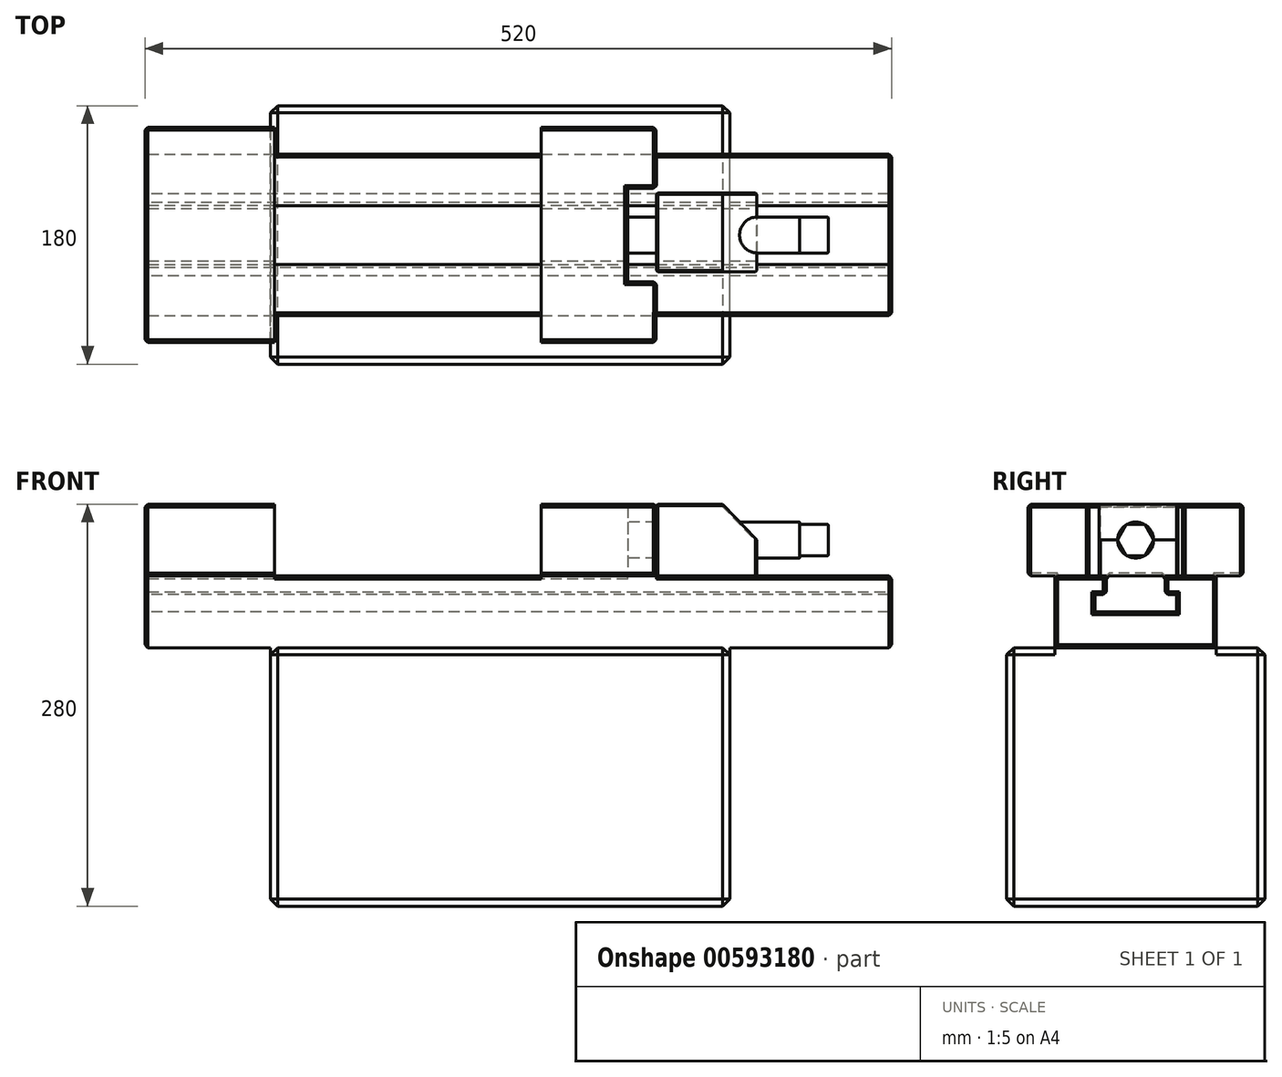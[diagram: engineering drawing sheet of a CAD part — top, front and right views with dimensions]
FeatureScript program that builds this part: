
annotation { "Feature Type Name" : "Feature", "Feature Type Description" : "" }
export const myFeature = defineFeature(function(context is Context, id is Id, definition is map)
    precondition{}
    {
        {
            var Q0;
            Q0=qCreatedBy(makeId("Top.planeOp"),FACE);
            var sketch = newSketch(context, id + "F0", { "sketchPlane" : qUnion([Q0])});
            skLineSegment(sketch, "E0.bottom", {"start": v(-189.84, -90) * mm, "end": v(130.16, -90) * mm});
            skLineSegment(sketch, "E0.top", {"start": v(-189.84, 90) * mm, "end": v(130.16, 90) * mm});
            skLineSegment(sketch, "E0.left", {"start": v(-189.84, -90) * mm, "end": v(-189.84, 90) * mm});
            skLineSegment(sketch, "E0.right", {"start": v(130.16, -90) * mm, "end": v(130.16, 90) * mm});
            skSolve(sketch);
        }
        {
            var Q0;
            Q0 = qSketchRegion(id + "F0", true);
            extrude(context, id + "F1", {"entities" : qUnion([Q0]), "depth" : 180 * mm, "offsetDistance" : 25 * mm});
        }
        {
            var Q0;
            Q0=makeQuery(id+"F1.opExtrude","CAP_FACE",FACE,{"disambiguationData":[OSD([sQuery(id+"F0.wireOp",EDGE,"E0.bottom"),sQuery(id+"F0.wireOp",EDGE,"E0.top"),sQuery(id+"F0.wireOp",EDGE,"E0.left"),sQuery(id+"F0.wireOp",EDGE,"E0.right")])],"isStart":false});
            var sketch = newSketch(context, id + "F2", { "sketchPlane" : qUnion([Q0])});
            skLineSegment(sketch, "E1.bottom", {"start": v(-277.14, -56.25) * mm, "end": v(242.86, -56.25) * mm});
            skLineSegment(sketch, "E1.top", {"start": v(-277.14, 56.25) * mm, "end": v(242.86, 56.25) * mm});
            skLineSegment(sketch, "E1.left", {"start": v(-277.14, -56.25) * mm, "end": v(-277.14, 56.25) * mm});
            skLineSegment(sketch, "E1.right", {"start": v(242.86, -56.25) * mm, "end": v(242.86, 56.25) * mm});
            skSolve(sketch);
        }
        {
            var Q0;
            Q0 = qSketchRegion(id + "F2", true);
            extrude(context, id + "F3", {"entities" : qUnion([Q0]), "operationType" : NewBodyOperationType.ADD, "depth" : 50 * mm, "offsetDistance" : 25 * mm});
        }
        {
            var Q0;
            Q0=makeQuery(id+"F3.opExtrude","CAP_FACE",FACE,{"disambiguationData":[OSD([sQuery(id+"F2.wireOp",EDGE,"E1.bottom"),sQuery(id+"F2.wireOp",EDGE,"E1.top"),sQuery(id+"F2.wireOp",EDGE,"E1.left"),sQuery(id+"F2.wireOp",EDGE,"E1.right")])],"isStart":false});
            var sketch = newSketch(context, id + "F4", { "sketchPlane" : qUnion([Q0])});
            skLineSegment(sketch, "E2.bottom", {"start": v(-277.14, -75) * mm, "end": v(-187.14, -75) * mm});
            skLineSegment(sketch, "E2.top", {"start": v(-277.14, 75) * mm, "end": v(-187.14, 75) * mm});
            skLineSegment(sketch, "E2.left", {"start": v(-277.14, -75) * mm, "end": v(-277.14, 75) * mm});
            skLineSegment(sketch, "E2.right", {"start": v(-187.14, -75) * mm, "end": v(-187.14, 75) * mm});
            skSolve(sketch);
        }
        {
            var Q0;
            Q0 = qSketchRegion(id + "F4", true);
            extrude(context, id + "F5", {"entities" : qUnion([Q0]), "operationType" : NewBodyOperationType.ADD, "depth" : 50 * mm, "offsetDistance" : 25 * mm});
        }
        {
            var Q0;
            {var subQ5=sQuery(id+"F2.wireOp",EDGE,"E1.top");var subQ6=sQuery(id+"F2.wireOp",EDGE,"E1.right");var subQ7=sQuery(id+"F2.wireOp",EDGE,"E1.bottom");Q0=makeQuery(id+"F11.boolean.opBoolean","SPLIT",FACE,{"disambiguationData":[TD([makeQuery(id+"F3.opExtrude","SWEPT_FACE",FACE,{"disambiguationData":[OSD([subQ6])]})])],"derivedFrom":makeQuery(id+"F3.opExtrude","CAP_FACE",FACE,{"disambiguationData":[OSD([subQ7,subQ5,sQuery(id+"F2.wireOp",EDGE,"E1.left"),subQ6])],"isStart":false})});}
            var sketch = newSketch(context, id + "F6", { "sketchPlane" : qUnion([Q0])});
            skLineSegment(sketch, "E3.bottom", {"start": v(78.92, 29.42) * mm, "end": v(148.92, 29.42) * mm});
            skLineSegment(sketch, "E3.top", {"start": v(78.92, -25.58) * mm, "end": v(148.92, -25.58) * mm});
            skLineSegment(sketch, "E3.left", {"start": v(78.92, 29.42) * mm, "end": v(78.92, -25.58) * mm});
            skLineSegment(sketch, "E3.right", {"start": v(148.92, 29.42) * mm, "end": v(148.92, -25.58) * mm});
            skSolve(sketch);
        }
        {
            var Q0;
            Q0 = qSketchRegion(id + "F6", true);
            extrude(context, id + "F7", {"entities" : qUnion([Q0]), "operationType" : NewBodyOperationType.ADD, "depth" : 50 * mm, "offsetDistance" : 25 * mm});
        }
        {
            var Q0;
            Q0=makeQuery(id+"F7.opExtrude","SWEPT_FACE",FACE,{"disambiguationData":[OSD([sQuery(id+"F6.wireOp",EDGE,"E3.top")])]});
            var sketch = newSketch(context, id + "F8", { "sketchPlane" : qUnion([Q0])});
            skLineSegment(sketch, "E4", {"start": v(125, 280) * mm, "end": v(148.92, 255) * mm});
            skLineSegment(sketch, "E5", {"start": v(148.92, 255) * mm, "end": v(148.92, 280) * mm});
            skLineSegment(sketch, "E6", {"start": v(148.92, 280) * mm, "end": v(125, 280) * mm});
            skSolve(sketch);
        }
        {
            var Q0;
            Q0 = qSketchRegion(id + "F8", true);
            extrude(context, id + "F9", {"entities" : qUnion([Q0]), "operationType" : NewBodyOperationType.REMOVE, "endBound" : BoundingType.THROUGH_ALL, "oppositeDirection" : true, "depth" : 25 * mm, "offsetDistance" : 25 * mm});
        }
        {
            var Q0;
            Q0=makeQuery(id+"F3.opExtrude","CAP_FACE",FACE,{"disambiguationData":[OSD([sQuery(id+"F2.wireOp",EDGE,"E1.bottom"),sQuery(id+"F2.wireOp",EDGE,"E1.top"),sQuery(id+"F2.wireOp",EDGE,"E1.left"),sQuery(id+"F2.wireOp",EDGE,"E1.right")])],"isStart":false});
            var sketch = newSketch(context, id + "F10", { "sketchPlane" : qUnion([Q0])});
            skLineSegment(sketch, "E7.bottom", {"start": v(-1.14, -75) * mm, "end": v(78.86, -75) * mm});
            skLineSegment(sketch, "E7.top", {"start": v(-1.14, 75) * mm, "end": v(78.86, 75) * mm});
            skLineSegment(sketch, "E7.left", {"start": v(-1.14, -75) * mm, "end": v(-1.14, 75) * mm});
            skLineSegment(sketch, "E8", {"start": v(58.92, -32.5) * mm, "end": v(79.04, -32.5) * mm});
            skLineSegment(sketch, "E9", {"start": v(58.92, -32.5) * mm, "end": v(58.92, 32.5) * mm});
            skLineSegment(sketch, "E10", {"start": v(58.92, 32.5) * mm, "end": v(78.92, 32.5) * mm});
            skLineSegment(sketch, "E11.trimOffspring", {"start": v(78.92, 32.5) * mm, "end": v(78.86, 75) * mm});
            skLineSegment(sketch, "E12", {"start": v(78.86, -75) * mm, "end": v(79.04, -32.5) * mm});
            skSolve(sketch);
        }
        {
            var Q0;
            Q0 = qSketchRegion(id + "F10", true);
            extrude(context, id + "F11", {"entities" : qUnion([Q0]), "operationType" : NewBodyOperationType.ADD, "depth" : 50 * mm, "offsetDistance" : 25 * mm});
        }
        {
            var Q0;
            Q0=makeQuery(id+"F11.opExtrude","SWEPT_FACE",FACE,{"disambiguationData":[OSD([sQuery(id+"F10.wireOp",EDGE,"E9")])]});
            var sketch = newSketch(context, id + "F12", { "sketchPlane" : qUnion([Q0])});
            skLineSegment(sketch, "E13", {"start": v(-32.5, 230) * mm, "end": v(32.5, 280) * mm});
            skCircle(sketch, "E14", {"center": v(0, 255) * mm, "radius": 12.5 * mm});
            skSolve(sketch);
        }
        {
            var Q0;
            Q0 = qSketchRegion(id + "F12", true);
            extrude(context, id + "F13", {"entities" : qUnion([Q0]), "operationType" : NewBodyOperationType.ADD, "depth" : 120 * mm, "offsetDistance" : 25 * mm});
        }
        {
            var Q0;
            Q0=makeQuery(id+"F13.opExtrude","CAP_FACE",FACE,{"disambiguationData":[OSD([sQuery(id+"F12.wireOp",EDGE,"E14")])],"isStart":false});
            var sketch = newSketch(context, id + "F14", { "sketchPlane" : qUnion([Q0])});
            skCircle(sketch, "E15.cCircle", {"center": v(0, 255) * mm, "radius": 11 * mm, "construction": true});
            skLineSegment(sketch, "E15.0", {"start": v(6.35, 244) * mm, "end": v(-6.35, 244) * mm});
            skLineSegment(sketch, "E15.1", {"start": v(-6.35, 244) * mm, "end": v(-12.7, 255) * mm});
            skLineSegment(sketch, "E15.2", {"start": v(-12.7, 255) * mm, "end": v(-6.35, 266) * mm});
            skLineSegment(sketch, "E15.3", {"start": v(-6.35, 266) * mm, "end": v(6.35, 266) * mm});
            skLineSegment(sketch, "E15.4", {"start": v(6.35, 266) * mm, "end": v(12.7, 255) * mm});
            skLineSegment(sketch, "E15.5", {"start": v(12.7, 255) * mm, "end": v(6.35, 244) * mm});
            skPoint(sketch, "E15.0.midPoint", {"position": v(0, 244) * mm});
            skSolve(sketch);
        }
        {
            var Q0;
            Q0 = qSketchRegion(id + "F14", true);
            extrude(context, id + "F15", {"entities" : qUnion([Q0]), "operationType" : NewBodyOperationType.ADD, "depth" : 20 * mm, "offsetDistance" : 25 * mm});
        }
        {
            var Q0;
            Q0=makeQuery(id+"F15.opExtrude","CAP_FACE",FACE,{"disambiguationData":[OSD([sQuery(id+"F14.wireOp",EDGE,"E15.0"),sQuery(id+"F14.wireOp",EDGE,"E15.1"),sQuery(id+"F14.wireOp",EDGE,"E15.2"),sQuery(id+"F14.wireOp",EDGE,"E15.3"),sQuery(id+"F14.wireOp",EDGE,"E15.4"),sQuery(id+"F14.wireOp",EDGE,"E15.5")])],"isStart":false});
            var Q1;
            Q1=makeQuery(id+"F15.opExtrude","SWEPT_EDGE",EDGE,{"disambiguationData":[OSD([sQuery(id+"F14.wireOp",EDGE,"E15.2"),sQuery(id+"F14.wireOp",EDGE,"E15.3")])]});
            var Q2;
            Q2=makeQuery(id+"F15.opExtrude","SWEPT_EDGE",EDGE,{"disambiguationData":[OSD([sQuery(id+"F14.wireOp",EDGE,"E15.1"),sQuery(id+"F14.wireOp",EDGE,"E15.2")])]});
            var Q3;
            Q3=makeQuery(id+"F15.opExtrude","SWEPT_EDGE",EDGE,{"disambiguationData":[OSD([sQuery(id+"F14.wireOp",EDGE,"E15.3"),sQuery(id+"F14.wireOp",EDGE,"E15.4")])]});
            var Q4;
            Q4=makeQuery(id+"F15.opExtrude","SWEPT_EDGE",EDGE,{"disambiguationData":[OSD([sQuery(id+"F14.wireOp",EDGE,"E15.0"),sQuery(id+"F14.wireOp",EDGE,"E15.1")])]});
            var Q5;
            Q5=makeQuery(id+"F15.opExtrude","SWEPT_EDGE",EDGE,{"disambiguationData":[OSD([sQuery(id+"F14.wireOp",EDGE,"E15.0"),sQuery(id+"F14.wireOp",EDGE,"E15.5")])]});
            var Q6;
            Q6=makeQuery(id+"F15.opExtrude","SWEPT_EDGE",EDGE,{"disambiguationData":[OSD([sQuery(id+"F14.wireOp",EDGE,"E15.4"),sQuery(id+"F14.wireOp",EDGE,"E15.5")])]});
            fillet(context, id + "F16", {"entities" : qUnion([Q0, Q1, Q2, Q3, Q4, Q5, Q6]), "radius" : 1 * mm, "tangentPropagation" : true, "allowEdgeOverflow" : false});
        }
        {
            var Q0;
            Q0=makeQuery(id+"F7.opExtrude","CAP_EDGE",EDGE,{"disambiguationData":[OSD([sQuery(id+"F6.wireOp",EDGE,"E3.top")])],"isStart":false});
            var Q1;
            Q1=makeQuery(id+"F9.boolean.opBoolean","COPY",EDGE,{"derivedFrom":makeQuery(id+"F9.opExtrude","CAP_EDGE",EDGE,{"disambiguationData":[OSD([sQuery(id+"F8.wireOp",EDGE,"E4")])],"isStart":true})});
            var Q2;
            Q2=makeQuery(id+"F7.opExtrude","SWEPT_EDGE",EDGE,{"disambiguationData":[OSD([sQuery(id+"F6.wireOp",EDGE,"E3.top"),sQuery(id+"F6.wireOp",EDGE,"E3.right")])]});
            var Q3;
            Q3=makeQuery(id+"F7.opExtrude","SWEPT_EDGE",EDGE,{"disambiguationData":[OSD([sQuery(id+"F6.wireOp",EDGE,"E3.top"),sQuery(id+"F6.wireOp",EDGE,"E3.left")])]});
            var Q4;
            Q4=makeQuery(id+"F7.opExtrude","CAP_EDGE",EDGE,{"disambiguationData":[OSD([sQuery(id+"F6.wireOp",EDGE,"E3.left")])],"isStart":false});
            var Q5;
            Q5=makeQuery(id+"F7.opExtrude","CAP_EDGE",EDGE,{"disambiguationData":[OSD([sQuery(id+"F6.wireOp",EDGE,"E3.bottom")])],"isStart":false});
            var Q6;
            Q6=makeQuery(id+"F9.boolean.opBoolean","INTERSECT",EDGE,{"derivedFrom":[makeQuery(id+"F7.opExtrude","SWEPT_FACE",FACE,{"disambiguationData":[OSD([sQuery(id+"F6.wireOp",EDGE,"E3.bottom")])]}),makeQuery(id+"F9.opExtrude","SWEPT_FACE",FACE,{"disambiguationData":[OSD([sQuery(id+"F8.wireOp",EDGE,"E4")])]})]});
            var Q7;
            Q7=makeQuery(id+"F7.opExtrude","SWEPT_EDGE",EDGE,{"disambiguationData":[OSD([sQuery(id+"F6.wireOp",EDGE,"E3.bottom"),sQuery(id+"F6.wireOp",EDGE,"E3.right")])]});
            var Q8;
            Q8=makeQuery(id+"F7.opExtrude","SWEPT_EDGE",EDGE,{"disambiguationData":[OSD([sQuery(id+"F6.wireOp",EDGE,"E3.bottom"),sQuery(id+"F6.wireOp",EDGE,"E3.left")])]});
            chamfer(context, id + "F17", {"entities" : qUnion([Q0, Q1, Q2, Q3, Q4, Q5, Q6, Q7, Q8]), "width" : 1 * mm, "tangentPropagation" : true});
        }
        {
            var Q0;
            Q0=makeQuery(id+"F1.opExtrude","CAP_EDGE",EDGE,{"disambiguationData":[OSD([sQuery(id+"F0.wireOp",EDGE,"E0.bottom")])],"isStart":false});
            var Q1;
            Q1=makeQuery(id+"F1.opExtrude","SWEPT_EDGE",EDGE,{"disambiguationData":[OSD([sQuery(id+"F0.wireOp",EDGE,"E0.bottom"),sQuery(id+"F0.wireOp",EDGE,"E0.right")])]});
            var Q2;
            {var subQ1=sQuery(id+"F0.wireOp",EDGE,"E0.right");var subQ2=makeQuery(id+"F1.opExtrude","SWEPT_FACE",FACE,{"disambiguationData":[OSD([subQ1])]});var subQ3=sQuery(id+"F0.wireOp",EDGE,"E0.bottom");var subQ4=makeQuery(id+"F1.opExtrude","CAP_FACE",FACE,{"disambiguationData":[OSD([subQ3,sQuery(id+"F0.wireOp",EDGE,"E0.top"),sQuery(id+"F0.wireOp",EDGE,"E0.left"),subQ1])],"isStart":false});Q2=makeQuery(id+"F3.boolean.opBoolean","SPLIT",EDGE,{"disambiguationData":[topologyDisambiguationEdgeConnected([subQ4,subQ2]),TD([makeQuery(id+"F1.opExtrude","SWEPT_FACE",FACE,{"disambiguationData":[OSD([subQ3])]})])],"derivedFrom":makeQuery(id+"F1.opExtrude","CAP_EDGE",EDGE,{"disambiguationData":[OSD([subQ1])],"isStart":false})});}
            var Q3;
            {var subQ1=sQuery(id+"F0.wireOp",EDGE,"E0.right");var subQ2=makeQuery(id+"F1.opExtrude","SWEPT_FACE",FACE,{"disambiguationData":[OSD([subQ1])]});var subQ3=sQuery(id+"F0.wireOp",EDGE,"E0.top");var subQ4=makeQuery(id+"F1.opExtrude","CAP_FACE",FACE,{"disambiguationData":[OSD([sQuery(id+"F0.wireOp",EDGE,"E0.bottom"),subQ3,sQuery(id+"F0.wireOp",EDGE,"E0.left"),subQ1])],"isStart":false});Q3=makeQuery(id+"F3.boolean.opBoolean","SPLIT",EDGE,{"disambiguationData":[topologyDisambiguationEdgeConnected([subQ4,subQ2]),TD([makeQuery(id+"F1.opExtrude","SWEPT_FACE",FACE,{"disambiguationData":[OSD([subQ3])]})])],"derivedFrom":makeQuery(id+"F1.opExtrude","CAP_EDGE",EDGE,{"disambiguationData":[OSD([subQ1])],"isStart":false})});}
            var Q4;
            Q4=makeQuery(id+"F1.opExtrude","SWEPT_EDGE",EDGE,{"disambiguationData":[OSD([sQuery(id+"F0.wireOp",EDGE,"E0.top"),sQuery(id+"F0.wireOp",EDGE,"E0.right")])]});
            var Q5;
            Q5=makeQuery(id+"F1.opExtrude","CAP_EDGE",EDGE,{"disambiguationData":[OSD([sQuery(id+"F0.wireOp",EDGE,"E0.top")])],"isStart":false});
            var Q6;
            Q6=makeQuery(id+"F1.opExtrude","CAP_EDGE",EDGE,{"disambiguationData":[OSD([sQuery(id+"F0.wireOp",EDGE,"E0.right")])],"isStart":true});
            var Q7;
            Q7=makeQuery(id+"F1.opExtrude","CAP_EDGE",EDGE,{"disambiguationData":[OSD([sQuery(id+"F0.wireOp",EDGE,"E0.bottom")])],"isStart":true});
            var Q8;
            Q8=makeQuery(id+"F1.opExtrude","SWEPT_EDGE",EDGE,{"disambiguationData":[OSD([sQuery(id+"F0.wireOp",EDGE,"E0.bottom"),sQuery(id+"F0.wireOp",EDGE,"E0.left")])]});
            var Q9;
            Q9=makeQuery(id+"F1.opExtrude","CAP_EDGE",EDGE,{"disambiguationData":[OSD([sQuery(id+"F0.wireOp",EDGE,"E0.left")])],"isStart":true});
            var Q10;
            Q10=makeQuery(id+"F1.opExtrude","CAP_EDGE",EDGE,{"disambiguationData":[OSD([sQuery(id+"F0.wireOp",EDGE,"E0.top")])],"isStart":true});
            var Q11;
            Q11=makeQuery(id+"F1.opExtrude","SWEPT_EDGE",EDGE,{"disambiguationData":[OSD([sQuery(id+"F0.wireOp",EDGE,"E0.top"),sQuery(id+"F0.wireOp",EDGE,"E0.left")])]});
            var Q12;
            {var subQ1=sQuery(id+"F0.wireOp",EDGE,"E0.left");var subQ2=makeQuery(id+"F1.opExtrude","SWEPT_FACE",FACE,{"disambiguationData":[OSD([subQ1])]});var subQ3=sQuery(id+"F0.wireOp",EDGE,"E0.top");var subQ4=makeQuery(id+"F1.opExtrude","CAP_FACE",FACE,{"disambiguationData":[OSD([sQuery(id+"F0.wireOp",EDGE,"E0.bottom"),subQ3,subQ1,sQuery(id+"F0.wireOp",EDGE,"E0.right")])],"isStart":false});Q12=makeQuery(id+"F3.boolean.opBoolean","SPLIT",EDGE,{"disambiguationData":[topologyDisambiguationEdgeConnected([subQ4,subQ2]),TD([makeQuery(id+"F1.opExtrude","SWEPT_FACE",FACE,{"disambiguationData":[OSD([subQ3])]})])],"derivedFrom":makeQuery(id+"F1.opExtrude","CAP_EDGE",EDGE,{"disambiguationData":[OSD([subQ1])],"isStart":false})});}
            var Q13;
            {var subQ1=sQuery(id+"F0.wireOp",EDGE,"E0.left");var subQ2=makeQuery(id+"F1.opExtrude","SWEPT_FACE",FACE,{"disambiguationData":[OSD([subQ1])]});var subQ3=sQuery(id+"F0.wireOp",EDGE,"E0.bottom");var subQ4=makeQuery(id+"F1.opExtrude","CAP_FACE",FACE,{"disambiguationData":[OSD([subQ3,sQuery(id+"F0.wireOp",EDGE,"E0.top"),subQ1,sQuery(id+"F0.wireOp",EDGE,"E0.right")])],"isStart":false});Q13=makeQuery(id+"F3.boolean.opBoolean","SPLIT",EDGE,{"disambiguationData":[topologyDisambiguationEdgeConnected([subQ4,subQ2]),TD([makeQuery(id+"F1.opExtrude","SWEPT_FACE",FACE,{"disambiguationData":[OSD([subQ3])]})])],"derivedFrom":makeQuery(id+"F1.opExtrude","CAP_EDGE",EDGE,{"disambiguationData":[OSD([subQ1])],"isStart":false})});}
            chamfer(context, id + "F18", {"entities" : qUnion([Q0, Q1, Q2, Q3, Q4, Q5, Q6, Q7, Q8, Q9, Q10, Q11, Q12, Q13]), "width" : 5 * mm, "tangentPropagation" : true});
        }
        {
            var Q0;
            Q0=makeQuery(id+"F5.boolean.opBoolean","MERGE",FACE,{"derivedFrom":[makeQuery(id+"F3.opExtrude","SWEPT_FACE",FACE,{"disambiguationData":[OSD([sQuery(id+"F2.wireOp",EDGE,"E1.left")])]}),makeQuery(id+"F5.opExtrude","SWEPT_FACE",FACE,{"disambiguationData":[OSD([sQuery(id+"F4.wireOp",EDGE,"E2.left")])]})]});
            var sketch = newSketch(context, id + "F19", { "sketchPlane" : qUnion([Q0])});
            skLineSegment(sketch, "E16", {"start": v(-20.5, 230) * mm, "end": v(20.5, 230) * mm});
            skLineSegment(sketch, "E17", {"start": v(20.5, 230) * mm, "end": v(20.5, 217) * mm});
            skLineSegment(sketch, "E18", {"start": v(20.5, 217) * mm, "end": v(28.5, 217) * mm});
            skLineSegment(sketch, "E19", {"start": v(28.5, 217) * mm, "end": v(28.5, 205) * mm});
            skLineSegment(sketch, "E20", {"start": v(28.5, 205) * mm, "end": v(-28.5, 205) * mm});
            skLineSegment(sketch, "E21", {"start": v(-28.5, 205) * mm, "end": v(-28.5, 217) * mm});
            skLineSegment(sketch, "E22", {"start": v(-28.5, 217) * mm, "end": v(-20.5, 217) * mm});
            skLineSegment(sketch, "E23", {"start": v(-20.5, 217) * mm, "end": v(-20.5, 230) * mm});
            skSolve(sketch);
        }
        {
            var Q0;
            Q0 = qSketchRegion(id + "F19", true);
            extrude(context, id + "F20", {"entities" : qUnion([Q0]), "operationType" : NewBodyOperationType.REMOVE, "endBound" : BoundingType.THROUGH_ALL, "oppositeDirection" : true, "depth" : 25 * mm, "offsetDistance" : 25 * mm});
        }
        {
            var Q0;
            Q0=makeQuery(id+"F3.opExtrude","SWEPT_FACE",FACE,{"disambiguationData":[OSD([sQuery(id+"F2.wireOp",EDGE,"E1.right")])]});
            var Q1;
            Q1=makeQuery(id+"F5.boolean.opBoolean","MERGE",FACE,{"derivedFrom":[makeQuery(id+"F3.opExtrude","SWEPT_FACE",FACE,{"disambiguationData":[OSD([sQuery(id+"F2.wireOp",EDGE,"E1.left")])]}),makeQuery(id+"F5.opExtrude","SWEPT_FACE",FACE,{"disambiguationData":[OSD([sQuery(id+"F4.wireOp",EDGE,"E2.left")])]})]});
            var Q2;
            Q2=makeQuery(id+"F5.opExtrude","CAP_EDGE",EDGE,{"disambiguationData":[OSD([sQuery(id+"F4.wireOp",EDGE,"E2.top")])],"isStart":false});
            var Q3;
            Q3=makeQuery(id+"F5.opExtrude","CAP_EDGE",EDGE,{"disambiguationData":[OSD([sQuery(id+"F4.wireOp",EDGE,"E2.bottom")])],"isStart":false});
            var Q4;
            Q4=makeQuery(id+"F11.opExtrude","CAP_EDGE",EDGE,{"disambiguationData":[OSD([sQuery(id+"F10.wireOp",EDGE,"E7.top")])],"isStart":false});
            var Q5;
            Q5=makeQuery(id+"F11.opExtrude","CAP_EDGE",EDGE,{"disambiguationData":[OSD([sQuery(id+"F10.wireOp",EDGE,"E11.trimOffspring")])],"isStart":false});
            var Q6;
            Q6=makeQuery(id+"F11.opExtrude","CAP_EDGE",EDGE,{"disambiguationData":[OSD([sQuery(id+"F10.wireOp",EDGE,"E10")])],"isStart":false});
            var Q7;
            Q7=makeQuery(id+"F11.opExtrude","CAP_EDGE",EDGE,{"disambiguationData":[OSD([sQuery(id+"F10.wireOp",EDGE,"E9")])],"isStart":false});
            var Q8;
            Q8=makeQuery(id+"F11.opExtrude","CAP_EDGE",EDGE,{"disambiguationData":[OSD([sQuery(id+"F10.wireOp",EDGE,"E8")])],"isStart":false});
            var Q9;
            Q9=makeQuery(id+"F11.opExtrude","CAP_EDGE",EDGE,{"disambiguationData":[OSD([sQuery(id+"F10.wireOp",EDGE,"E12")])],"isStart":false});
            var Q10;
            Q10=makeQuery(id+"F11.opExtrude","CAP_EDGE",EDGE,{"disambiguationData":[OSD([sQuery(id+"F10.wireOp",EDGE,"E7.bottom")])],"isStart":false});
            var Q11;
            Q11=makeQuery(id+"F5.opExtrude","CAP_EDGE",EDGE,{"disambiguationData":[OSD([sQuery(id+"F4.wireOp",EDGE,"E2.bottom")])],"isStart":true});
            var Q12;
            Q12=makeQuery(id+"F11.opExtrude","CAP_EDGE",EDGE,{"disambiguationData":[OSD([sQuery(id+"F10.wireOp",EDGE,"E7.bottom")])],"isStart":true});
            var Q13;
            Q13=makeQuery(id+"F11.opExtrude","SWEPT_EDGE",EDGE,{"disambiguationData":[OSD([sQuery(id+"F10.wireOp",EDGE,"E7.bottom"),sQuery(id+"F10.wireOp",EDGE,"E12")])]});
            var Q14;
            Q14=makeQuery(id+"F11.opExtrude","SWEPT_EDGE",EDGE,{"disambiguationData":[OSD([sQuery(id+"F10.wireOp",EDGE,"E8"),sQuery(id+"F10.wireOp",EDGE,"E12")])]});
            var Q15;
            Q15=makeQuery(id+"F11.opExtrude","SWEPT_EDGE",EDGE,{"disambiguationData":[OSD([sQuery(id+"F10.wireOp",EDGE,"E10"),sQuery(id+"F10.wireOp",EDGE,"E11.trimOffspring")])]});
            var Q16;
            Q16=makeQuery(id+"F11.opExtrude","SWEPT_EDGE",EDGE,{"disambiguationData":[OSD([sQuery(id+"F10.wireOp",EDGE,"E7.top"),sQuery(id+"F10.wireOp",EDGE,"E11.trimOffspring")])]});
            var Q17;
            Q17=makeQuery(id+"F11.opExtrude","CAP_EDGE",EDGE,{"disambiguationData":[OSD([sQuery(id+"F10.wireOp",EDGE,"E7.top")])],"isStart":true});
            var Q18;
            Q18=makeQuery(id+"F5.opExtrude","CAP_EDGE",EDGE,{"disambiguationData":[OSD([sQuery(id+"F4.wireOp",EDGE,"E2.top")])],"isStart":true});
            var Q19;
            {var subQ0=sQuery(id+"F19.wireOp",EDGE,"E16");var subQ1=sQuery(id+"F2.wireOp",EDGE,"E1.right");var subQ2=makeQuery(id+"F3.opExtrude","CAP_FACE",FACE,{"disambiguationData":[OSD([sQuery(id+"F2.wireOp",EDGE,"E1.bottom"),sQuery(id+"F2.wireOp",EDGE,"E1.top"),sQuery(id+"F2.wireOp",EDGE,"E1.left"),subQ1])],"isStart":false});var subQ3=sQuery(id+"F19.wireOp",EDGE,"E17");var subQ4=makeQuery(id+"F20.opExtrude","SWEPT_FACE",FACE,{"disambiguationData":[OSD([subQ3])]});Q19=makeQuery(id+"F20.boolean.opBoolean","COPY",EDGE,{"disambiguationData":[topologyDisambiguationEdgeConnected([subQ2,subQ4]),TD([makeQuery(id+"F3.opExtrude","SWEPT_FACE",FACE,{"disambiguationData":[OSD([subQ1])]})])],"derivedFrom":makeQuery(id+"F20.opExtrude","SWEPT_EDGE",EDGE,{"disambiguationData":[OSD([subQ0,subQ3])]})});}
            var Q20;
            {var subQ0=sQuery(id+"F19.wireOp",EDGE,"E16");var subQ1=sQuery(id+"F2.wireOp",EDGE,"E1.right");var subQ2=makeQuery(id+"F3.opExtrude","CAP_FACE",FACE,{"disambiguationData":[OSD([sQuery(id+"F2.wireOp",EDGE,"E1.bottom"),sQuery(id+"F2.wireOp",EDGE,"E1.top"),sQuery(id+"F2.wireOp",EDGE,"E1.left"),subQ1])],"isStart":false});var subQ3=sQuery(id+"F19.wireOp",EDGE,"E23");var subQ4=makeQuery(id+"F20.opExtrude","SWEPT_FACE",FACE,{"disambiguationData":[OSD([subQ3])]});Q20=makeQuery(id+"F20.boolean.opBoolean","COPY",EDGE,{"disambiguationData":[topologyDisambiguationEdgeConnected([subQ2,subQ4]),TD([makeQuery(id+"F3.opExtrude","SWEPT_FACE",FACE,{"disambiguationData":[OSD([subQ1])]})])],"derivedFrom":makeQuery(id+"F20.opExtrude","SWEPT_EDGE",EDGE,{"disambiguationData":[OSD([subQ0,subQ3])]})});}
            var Q21;
            {var subQ0=sQuery(id+"F19.wireOp",EDGE,"E16");var subQ1=makeQuery(id+"F3.opExtrude","CAP_FACE",FACE,{"disambiguationData":[OSD([sQuery(id+"F2.wireOp",EDGE,"E1.bottom"),sQuery(id+"F2.wireOp",EDGE,"E1.top"),sQuery(id+"F2.wireOp",EDGE,"E1.left"),sQuery(id+"F2.wireOp",EDGE,"E1.right")])],"isStart":false});var subQ2=sQuery(id+"F19.wireOp",EDGE,"E17");var subQ3=makeQuery(id+"F20.opExtrude","SWEPT_FACE",FACE,{"disambiguationData":[OSD([subQ2])]});Q21=makeQuery(id+"F20.boolean.opBoolean","COPY",EDGE,{"disambiguationData":[topologyDisambiguationEdgeConnected([subQ1,subQ3]),TD([makeQuery(id+"F5.opExtrude","SWEPT_FACE",FACE,{"disambiguationData":[OSD([sQuery(id+"F4.wireOp",EDGE,"E2.right")])]})])],"derivedFrom":makeQuery(id+"F20.opExtrude","SWEPT_EDGE",EDGE,{"disambiguationData":[OSD([subQ0,subQ2])]})});}
            var Q22;
            {var subQ0=sQuery(id+"F19.wireOp",EDGE,"E16");var subQ1=makeQuery(id+"F3.opExtrude","CAP_FACE",FACE,{"disambiguationData":[OSD([sQuery(id+"F2.wireOp",EDGE,"E1.bottom"),sQuery(id+"F2.wireOp",EDGE,"E1.top"),sQuery(id+"F2.wireOp",EDGE,"E1.left"),sQuery(id+"F2.wireOp",EDGE,"E1.right")])],"isStart":false});var subQ2=sQuery(id+"F19.wireOp",EDGE,"E23");var subQ3=makeQuery(id+"F20.opExtrude","SWEPT_FACE",FACE,{"disambiguationData":[OSD([subQ2])]});Q22=makeQuery(id+"F20.boolean.opBoolean","COPY",EDGE,{"disambiguationData":[topologyDisambiguationEdgeConnected([subQ1,subQ3]),TD([makeQuery(id+"F5.opExtrude","SWEPT_FACE",FACE,{"disambiguationData":[OSD([sQuery(id+"F4.wireOp",EDGE,"E2.right")])]})])],"derivedFrom":makeQuery(id+"F20.opExtrude","SWEPT_EDGE",EDGE,{"disambiguationData":[OSD([subQ0,subQ2])]})});}
            var Q23;
            {var subQ0=sQuery(id+"F4.wireOp",EDGE,"E2.right");var subQ1=sQuery(id+"F2.wireOp",EDGE,"E1.top");var subQ2=makeQuery(id+"F3.opExtrude","SWEPT_FACE",FACE,{"disambiguationData":[OSD([subQ1])]});var subQ4=makeQuery(id+"F3.opExtrude","CAP_FACE",FACE,{"disambiguationData":[OSD([sQuery(id+"F2.wireOp",EDGE,"E1.bottom"),subQ1,sQuery(id+"F2.wireOp",EDGE,"E1.left"),sQuery(id+"F2.wireOp",EDGE,"E1.right")])],"isStart":false});Q23=makeQuery(id+"F11.boolean.opBoolean","SPLIT",EDGE,{"disambiguationData":[topologyDisambiguationEdgeConnected([subQ4,subQ2]),TD([makeQuery(id+"F5.opExtrude","SWEPT_FACE",FACE,{"disambiguationData":[OSD([subQ0])]})])],"derivedFrom":makeQuery(id+"F5.boolean.opBoolean","SPLIT",EDGE,{"disambiguationData":[topologyDisambiguationEdgeConnected([subQ4])],"derivedFrom":makeQuery(id+"F3.opExtrude","CAP_EDGE",EDGE,{"disambiguationData":[OSD([subQ1])],"isStart":false})})});}
            var Q24;
            {var subQ1=sQuery(id+"F2.wireOp",EDGE,"E1.right");var subQ2=sQuery(id+"F2.wireOp",EDGE,"E1.top");var subQ3=makeQuery(id+"F3.opExtrude","SWEPT_FACE",FACE,{"disambiguationData":[OSD([subQ2])]});var subQ4=makeQuery(id+"F3.opExtrude","CAP_FACE",FACE,{"disambiguationData":[OSD([sQuery(id+"F2.wireOp",EDGE,"E1.bottom"),subQ2,sQuery(id+"F2.wireOp",EDGE,"E1.left"),subQ1])],"isStart":false});Q24=makeQuery(id+"F11.boolean.opBoolean","SPLIT",EDGE,{"disambiguationData":[topologyDisambiguationEdgeConnected([subQ4,subQ3]),TD([makeQuery(id+"F3.opExtrude","SWEPT_FACE",FACE,{"disambiguationData":[OSD([subQ1])]})])],"derivedFrom":makeQuery(id+"F5.boolean.opBoolean","SPLIT",EDGE,{"disambiguationData":[topologyDisambiguationEdgeConnected([subQ4])],"derivedFrom":makeQuery(id+"F3.opExtrude","CAP_EDGE",EDGE,{"disambiguationData":[OSD([subQ2])],"isStart":false})})});}
            var Q25;
            {var subQ0=sQuery(id+"F2.wireOp",EDGE,"E1.right");var subQ1=sQuery(id+"F2.wireOp",EDGE,"E1.bottom");var subQ2=makeQuery(id+"F3.opExtrude","CAP_FACE",FACE,{"disambiguationData":[OSD([subQ1,sQuery(id+"F2.wireOp",EDGE,"E1.top"),sQuery(id+"F2.wireOp",EDGE,"E1.left"),subQ0])],"isStart":false});var subQ4=makeQuery(id+"F3.opExtrude","SWEPT_FACE",FACE,{"disambiguationData":[OSD([subQ1])]});Q25=makeQuery(id+"F11.boolean.opBoolean","SPLIT",EDGE,{"disambiguationData":[topologyDisambiguationEdgeConnected([subQ4,subQ2]),TD([makeQuery(id+"F3.opExtrude","SWEPT_FACE",FACE,{"disambiguationData":[OSD([subQ0])]})])],"derivedFrom":makeQuery(id+"F5.boolean.opBoolean","SPLIT",EDGE,{"disambiguationData":[topologyDisambiguationEdgeConnected([subQ2])],"derivedFrom":makeQuery(id+"F3.opExtrude","CAP_EDGE",EDGE,{"disambiguationData":[OSD([subQ1])],"isStart":false})})});}
            var Q26;
            {var subQ0=sQuery(id+"F4.wireOp",EDGE,"E2.right");var subQ1=sQuery(id+"F2.wireOp",EDGE,"E1.bottom");var subQ2=makeQuery(id+"F3.opExtrude","CAP_FACE",FACE,{"disambiguationData":[OSD([subQ1,sQuery(id+"F2.wireOp",EDGE,"E1.top"),sQuery(id+"F2.wireOp",EDGE,"E1.left"),sQuery(id+"F2.wireOp",EDGE,"E1.right")])],"isStart":false});var subQ4=makeQuery(id+"F3.opExtrude","SWEPT_FACE",FACE,{"disambiguationData":[OSD([subQ1])]});Q26=makeQuery(id+"F11.boolean.opBoolean","SPLIT",EDGE,{"disambiguationData":[topologyDisambiguationEdgeConnected([subQ4,subQ2]),TD([makeQuery(id+"F5.opExtrude","SWEPT_FACE",FACE,{"disambiguationData":[OSD([subQ0])]})])],"derivedFrom":makeQuery(id+"F5.boolean.opBoolean","SPLIT",EDGE,{"disambiguationData":[topologyDisambiguationEdgeConnected([subQ2])],"derivedFrom":makeQuery(id+"F3.opExtrude","CAP_EDGE",EDGE,{"disambiguationData":[OSD([subQ1])],"isStart":false})})});}
            var Q27;
            Q27=makeQuery(id+"F20.boolean.opBoolean","COPY",EDGE,{"derivedFrom":makeQuery(id+"F20.opExtrude","SWEPT_EDGE",EDGE,{"disambiguationData":[OSD([sQuery(id+"F19.wireOp",EDGE,"E22"),sQuery(id+"F19.wireOp",EDGE,"E23")])]})});
            var Q28;
            Q28=makeQuery(id+"F20.boolean.opBoolean","COPY",EDGE,{"derivedFrom":makeQuery(id+"F20.opExtrude","SWEPT_EDGE",EDGE,{"disambiguationData":[OSD([sQuery(id+"F19.wireOp",EDGE,"E17"),sQuery(id+"F19.wireOp",EDGE,"E18")])]})});
            chamfer(context, id + "F21", {"entities" : qUnion([Q0, Q1, Q2, Q3, Q4, Q5, Q6, Q7, Q8, Q9, Q10, Q11, Q12, Q13, Q14, Q15, Q16, Q17, Q18, Q19, Q20, Q21, Q22, Q23, Q24, Q25, Q26, Q27, Q28]), "width" : 2 * mm, "tangentPropagation" : true});
        }
    });
